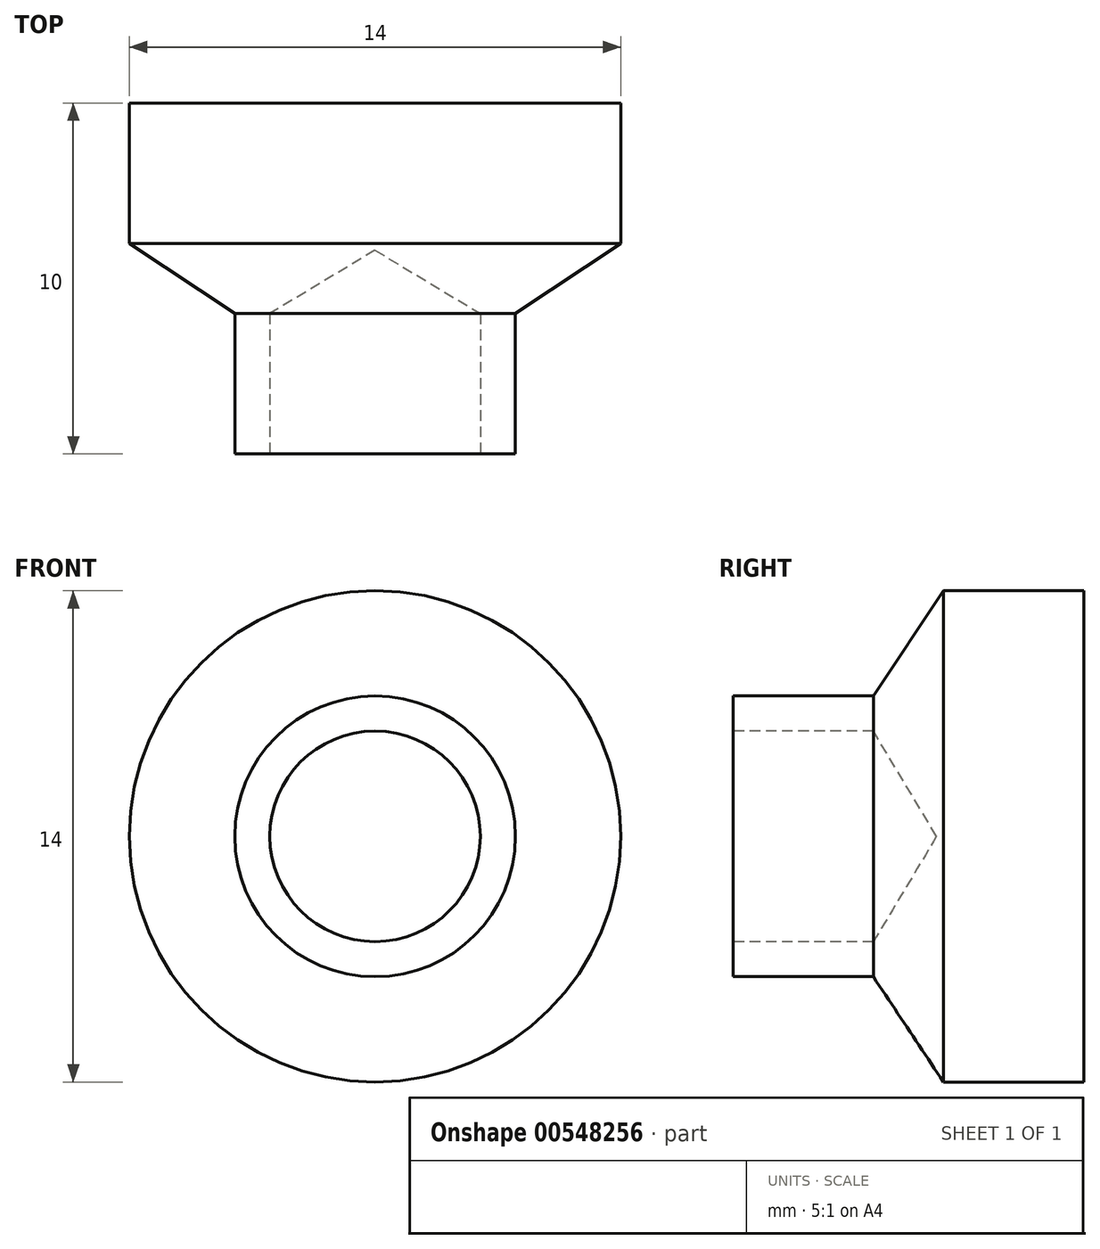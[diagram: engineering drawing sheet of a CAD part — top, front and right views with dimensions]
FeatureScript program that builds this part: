
annotation { "Feature Type Name" : "Feature", "Feature Type Description" : "" }
export const myFeature = defineFeature(function(context is Context, id is Id, definition is map)
    precondition{}
    {
        {
            var Q0;
            Q0=qCreatedBy(makeId("Right.planeOp"),FACE);
            var sketch = newSketch(context, id + "F0", { "sketchPlane" : qUnion([Q0])});
            skLineSegment(sketch, "E0", {"start": v(-4, 0) * mm, "end": v(6, 0) * mm});
            skLineSegment(sketch, "E1", {"start": v(6, 0) * mm, "end": v(6, 7) * mm});
            skLineSegment(sketch, "E2", {"start": v(6, 7) * mm, "end": v(2, 7) * mm});
            skLineSegment(sketch, "E3", {"start": v(2, 7) * mm, "end": v(0, 4) * mm});
            skLineSegment(sketch, "E4", {"start": v(0, 4) * mm, "end": v(-4, 4) * mm});
            skLineSegment(sketch, "E5", {"start": v(-4, 4) * mm, "end": v(-4, 0) * mm});
            skSolve(sketch);
        }
        {
            var Q0;
            Q0=makeQuery(id+"F0.imprint","IMPRINT",FACE,{"disambiguationData":[TD([[makeQuery(id+"F0.imprint","IMPRINT",EDGE,{"derivedFrom":sQuery(id+"F0.wireOp",EDGE,"E0")}),1.0]])]});
            var Q1;
            Q1=sQuery(id+"F0.wireOp",EDGE,"E0");
            revolve(context, id + "F1", {"entities" : qUnion([Q0]), "axis" : qUnion([Q1]), "revolveType" : RevolveType.FULL});
        }
        {
            var Q0;
            Q0=makeQuery(id+"F1.opRevolve","SWEPT_FACE",FACE,{"disambiguationData":[OSD([sQuery(id+"F0.wireOp",EDGE,"E5")])]});
            var sketch = newSketch(context, id + "F2", { "sketchPlane" : qUnion([Q0])});
            skPoint(sketch, "E6", {"position": v(0, 0) * mm});
            skSolve(sketch);
        }
        {
            var Q0;
            Q0=sQuery(id+"F2.wireOp",VERTEX,"E6");
            var Q1;
            Q1=makeQuery(id+"F1.opRevolve","SWEPT_BODY",BODY,{"disambiguationData":[OSD([sQuery(id+"F0.wireOp",EDGE,"E0"),sQuery(id+"F0.wireOp",EDGE,"E1"),sQuery(id+"F0.wireOp",EDGE,"E2"),sQuery(id+"F0.wireOp",EDGE,"E3"),sQuery(id+"F0.wireOp",EDGE,"E4"),sQuery(id+"F0.wireOp",EDGE,"E5")])]});
            hole(context, id + "F3", {"style" : HoleStyle.SIMPLE, "endStyle" : HoleEndStyle.BLIND, "holeDiameter" : 6 * mm, "holeDepth" : 4 * mm, "isTappedThrough" : true, "tappedDepth" : 12 * mm, "tapClearance" : 3, "locations" : qUnion([Q0]), "scope" : qUnion([Q1])});
        }
    });
